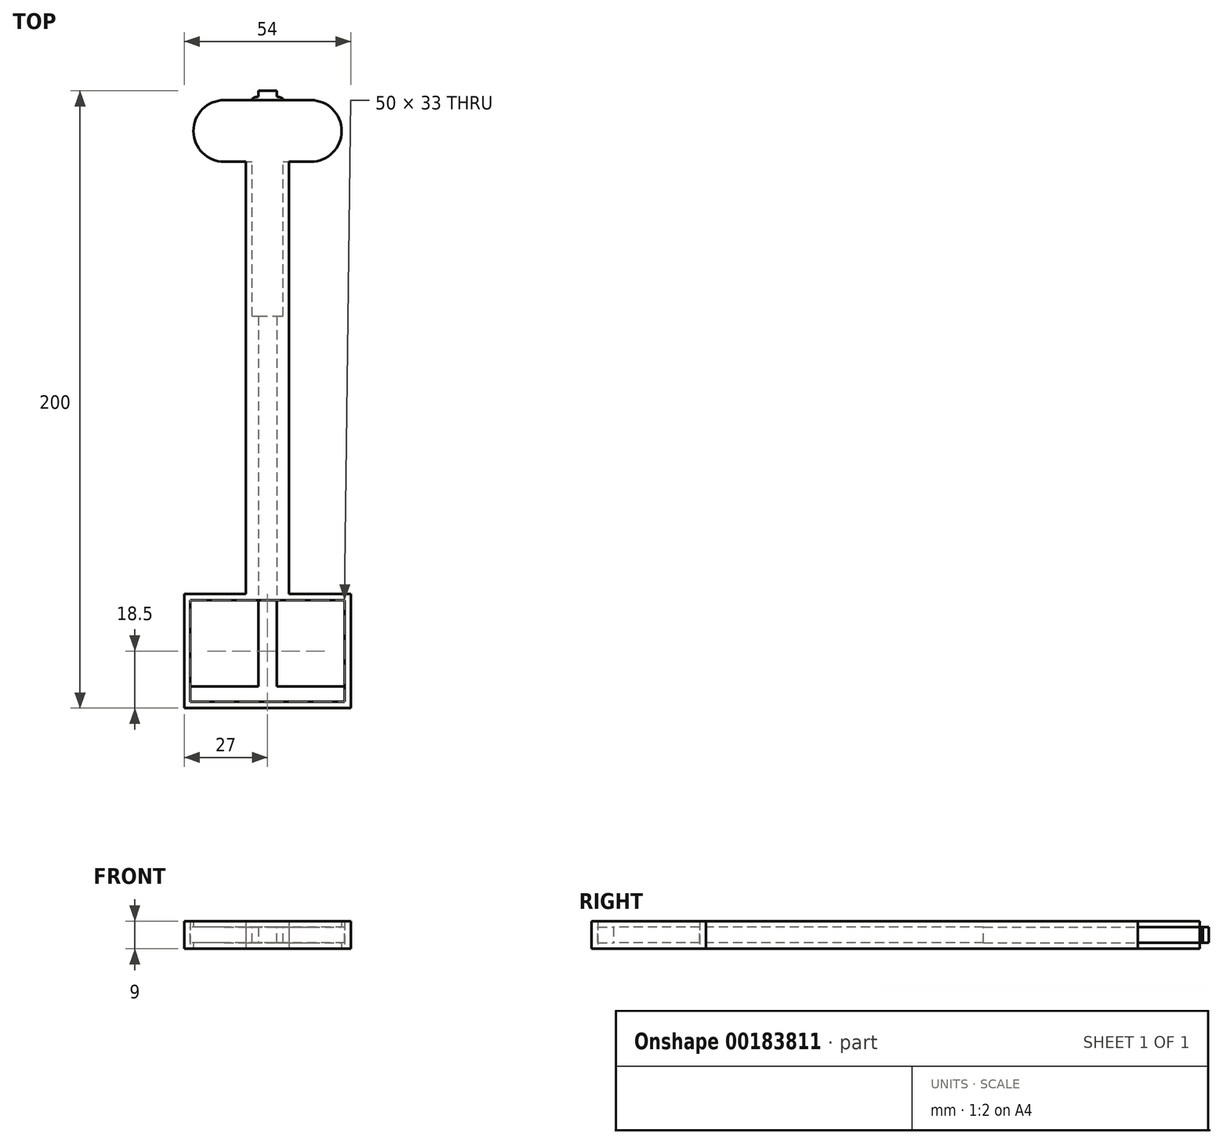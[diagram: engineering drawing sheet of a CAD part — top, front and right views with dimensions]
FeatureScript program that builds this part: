
annotation { "Feature Type Name" : "Feature", "Feature Type Description" : "" }
export const myFeature = defineFeature(function(context is Context, id is Id, definition is map)
    precondition{}
    {
        {
            var Q0;
            Q0=qCreatedBy(makeId("Top.planeOp"),FACE);
            var sketch = newSketch(context, id + "F0", { "sketchPlane" : qUnion([Q0])});
            skLineSegment(sketch, "E0.bottom", {"start": v(0, 13) * mm, "end": v(3, 13) * mm});
            skLineSegment(sketch, "E0.top", {"start": v(0, -180) * mm, "end": v(3, -180) * mm});
            skLineSegment(sketch, "E0.left", {"start": v(0, 13) * mm, "end": v(0, -180) * mm});
            skLineSegment(sketch, "E0.right", {"start": v(3, 13) * mm, "end": v(3, -180) * mm});
            skLineSegment(sketch, "E1", {"start": v(0, 10) * mm, "end": v(3, 10) * mm, "construction": true});
            skArc(sketch, "E2", {"start": v(3, 11.09) * mm, "mid": v(4.04, 10.94) * mm, "end": v(5, 10.5) * mm});
            skLineSegment(sketch, "E3", {"start": v(5, 10.5) * mm, "end": v(5, 10) * mm});
            skArc(sketch, "E4.MirrorCS", {"start": v(3, 8.91) * mm, "mid": v(4.04, 9.06) * mm, "end": v(5, 9.5) * mm});
            skLineSegment(sketch, "E5.MirrorCS", {"start": v(5, 9.5) * mm, "end": v(5, 10) * mm});
            skArc(sketch, "E6.1.0.0", {"start": v(3, 7.89) * mm, "mid": v(4.04, 7.74) * mm, "end": v(5, 7.3) * mm});
            skLineSegment(sketch, "E6.1.0.1", {"start": v(5, 7.3) * mm, "end": v(5, 6.8) * mm});
            skLineSegment(sketch, "E6.1.0.2", {"start": v(5, 6.3) * mm, "end": v(5, 6.8) * mm});
            skArc(sketch, "E6.1.0.3", {"start": v(3, 5.71) * mm, "mid": v(4.04, 5.86) * mm, "end": v(5, 6.3) * mm});
            skArc(sketch, "E6.2.0.0", {"start": v(3, 4.69) * mm, "mid": v(4.04, 4.54) * mm, "end": v(5, 4.1) * mm});
            skLineSegment(sketch, "E6.2.0.1", {"start": v(5, 4.1) * mm, "end": v(5, 3.6) * mm});
            skLineSegment(sketch, "E6.2.0.2", {"start": v(5, 3.1) * mm, "end": v(5, 3.6) * mm});
            skArc(sketch, "E6.2.0.3", {"start": v(3, 2.51) * mm, "mid": v(4.04, 2.66) * mm, "end": v(5, 3.1) * mm});
            skLineSegment(sketch, "E6.direction1", {"start": v(3, 7.39) * mm, "end": v(3, 4.19) * mm, "construction": true});
            skArc(sketch, "E7.0.3.0", {"start": v(3, 1.49) * mm, "mid": v(4.04, 1.34) * mm, "end": v(5, 0.9) * mm});
            skLineSegment(sketch, "E7.4.3.0", {"start": v(5, 0.9) * mm, "end": v(5, 0.4) * mm});
            skLineSegment(sketch, "E7.7.3.0", {"start": v(5, -0.1) * mm, "end": v(5, 0.4) * mm});
            skArc(sketch, "E7.10.3.0", {"start": v(3, -0.69) * mm, "mid": v(4.04, -0.54) * mm, "end": v(5, -0.1) * mm});
            skArc(sketch, "E7.0.4.0", {"start": v(3, -1.71) * mm, "mid": v(4.04, -1.86) * mm, "end": v(5, -2.3) * mm});
            skLineSegment(sketch, "E7.4.4.0", {"start": v(5, -2.3) * mm, "end": v(5, -2.8) * mm});
            skLineSegment(sketch, "E7.7.4.0", {"start": v(5, -3.3) * mm, "end": v(5, -2.8) * mm});
            skArc(sketch, "E7.10.4.0", {"start": v(3, -3.89) * mm, "mid": v(4.04, -3.74) * mm, "end": v(5, -3.3) * mm});
            skArc(sketch, "E7.0.5.0", {"start": v(3, -4.91) * mm, "mid": v(4.04, -5.06) * mm, "end": v(5, -5.5) * mm});
            skLineSegment(sketch, "E7.4.5.0", {"start": v(5, -5.5) * mm, "end": v(5, -6) * mm});
            skLineSegment(sketch, "E7.7.5.0", {"start": v(5, -6.5) * mm, "end": v(5, -6) * mm});
            skArc(sketch, "E7.10.5.0", {"start": v(3, -7.09) * mm, "mid": v(4.04, -6.94) * mm, "end": v(5, -6.5) * mm});
            skArc(sketch, "E7.0.6.0", {"start": v(3, -8.11) * mm, "mid": v(4.04, -8.26) * mm, "end": v(5, -8.7) * mm});
            skLineSegment(sketch, "E7.4.6.0", {"start": v(5, -8.7) * mm, "end": v(5, -9.2) * mm});
            skLineSegment(sketch, "E7.7.6.0", {"start": v(5, -9.7) * mm, "end": v(5, -9.2) * mm});
            skArc(sketch, "E7.10.6.0", {"start": v(3, -10.29) * mm, "mid": v(4.04, -10.14) * mm, "end": v(5, -9.7) * mm});
            skArc(sketch, "E7.0.7.0", {"start": v(3, -11.31) * mm, "mid": v(4.04, -11.46) * mm, "end": v(5, -11.9) * mm});
            skLineSegment(sketch, "E7.4.7.0", {"start": v(5, -11.9) * mm, "end": v(5, -12.4) * mm});
            skLineSegment(sketch, "E7.7.7.0", {"start": v(5, -12.9) * mm, "end": v(5, -12.4) * mm});
            skArc(sketch, "E7.10.7.0", {"start": v(3, -13.49) * mm, "mid": v(4.04, -13.34) * mm, "end": v(5, -12.9) * mm});
            skArc(sketch, "E7.0.8.0", {"start": v(3, -14.51) * mm, "mid": v(4.04, -14.66) * mm, "end": v(5, -15.1) * mm});
            skLineSegment(sketch, "E7.4.8.0", {"start": v(5, -15.1) * mm, "end": v(5, -15.6) * mm});
            skLineSegment(sketch, "E7.7.8.0", {"start": v(5, -16.1) * mm, "end": v(5, -15.6) * mm});
            skArc(sketch, "E7.10.8.0", {"start": v(3, -16.69) * mm, "mid": v(4.04, -16.54) * mm, "end": v(5, -16.1) * mm});
            skArc(sketch, "E7.0.9.0", {"start": v(3, -17.71) * mm, "mid": v(4.04, -17.86) * mm, "end": v(5, -18.3) * mm});
            skLineSegment(sketch, "E7.4.9.0", {"start": v(5, -18.3) * mm, "end": v(5, -18.8) * mm});
            skLineSegment(sketch, "E7.7.9.0", {"start": v(5, -19.3) * mm, "end": v(5, -18.8) * mm});
            skArc(sketch, "E7.10.9.0", {"start": v(3, -19.89) * mm, "mid": v(4.04, -19.74) * mm, "end": v(5, -19.3) * mm});
            skArc(sketch, "E7.0.10.0", {"start": v(3, -20.91) * mm, "mid": v(4.04, -21.06) * mm, "end": v(5, -21.5) * mm});
            skLineSegment(sketch, "E7.4.10.0", {"start": v(5, -21.5) * mm, "end": v(5, -22) * mm});
            skLineSegment(sketch, "E7.7.10.0", {"start": v(5, -22.5) * mm, "end": v(5, -22) * mm});
            skArc(sketch, "E7.10.10.0", {"start": v(3, -23.09) * mm, "mid": v(4.04, -22.94) * mm, "end": v(5, -22.5) * mm});
            skArc(sketch, "E7.0.11.0", {"start": v(3, -24.11) * mm, "mid": v(4.04, -24.26) * mm, "end": v(5, -24.7) * mm});
            skLineSegment(sketch, "E7.4.11.0", {"start": v(5, -24.7) * mm, "end": v(5, -25.2) * mm});
            skLineSegment(sketch, "E7.7.11.0", {"start": v(5, -25.7) * mm, "end": v(5, -25.2) * mm});
            skArc(sketch, "E7.10.11.0", {"start": v(3, -26.29) * mm, "mid": v(4.04, -26.14) * mm, "end": v(5, -25.7) * mm});
            skArc(sketch, "E7.0.12.0", {"start": v(3, -27.31) * mm, "mid": v(4.04, -27.46) * mm, "end": v(5, -27.9) * mm});
            skLineSegment(sketch, "E7.4.12.0", {"start": v(5, -27.9) * mm, "end": v(5, -28.4) * mm});
            skLineSegment(sketch, "E7.7.12.0", {"start": v(5, -28.9) * mm, "end": v(5, -28.4) * mm});
            skArc(sketch, "E7.10.12.0", {"start": v(3, -29.49) * mm, "mid": v(4.04, -29.34) * mm, "end": v(5, -28.9) * mm});
            skArc(sketch, "E7.0.13.0", {"start": v(3, -30.51) * mm, "mid": v(4.04, -30.66) * mm, "end": v(5, -31.1) * mm});
            skLineSegment(sketch, "E7.4.13.0", {"start": v(5, -31.1) * mm, "end": v(5, -31.6) * mm});
            skLineSegment(sketch, "E7.7.13.0", {"start": v(5, -32.1) * mm, "end": v(5, -31.6) * mm});
            skArc(sketch, "E7.10.13.0", {"start": v(3, -32.69) * mm, "mid": v(4.04, -32.54) * mm, "end": v(5, -32.1) * mm});
            skArc(sketch, "E7.0.14.0", {"start": v(3, -33.71) * mm, "mid": v(4.04, -33.86) * mm, "end": v(5, -34.3) * mm});
            skLineSegment(sketch, "E7.4.14.0", {"start": v(5, -34.3) * mm, "end": v(5, -34.8) * mm});
            skLineSegment(sketch, "E7.7.14.0", {"start": v(5, -35.3) * mm, "end": v(5, -34.8) * mm});
            skArc(sketch, "E7.10.14.0", {"start": v(3, -35.89) * mm, "mid": v(4.04, -35.74) * mm, "end": v(5, -35.3) * mm});
            skArc(sketch, "E7.0.15.0", {"start": v(3, -36.91) * mm, "mid": v(4.04, -37.06) * mm, "end": v(5, -37.5) * mm});
            skLineSegment(sketch, "E7.4.15.0", {"start": v(5, -37.5) * mm, "end": v(5, -38) * mm});
            skLineSegment(sketch, "E7.7.15.0", {"start": v(5, -38.5) * mm, "end": v(5, -38) * mm});
            skArc(sketch, "E7.10.15.0", {"start": v(3, -39.09) * mm, "mid": v(4.04, -38.94) * mm, "end": v(5, -38.5) * mm});
            skSolve(sketch);
        }
        {
            var Q0;
            Q0 = qSketchRegion(id + "F0", true);
            extrude(context, id + "F1", {"entities" : qUnion([Q0]), "depth" : 5 * mm});
        }
        {
            var Q0;
            Q0=makeQuery(id+"F1.opExtrude","SWEPT_BODY",BODY,{"disambiguationData":[OSD([sQuery(id+"F0.wireOp",EDGE,"E0.bottom"),sQuery(id+"F0.wireOp",EDGE,"E0.top"),sQuery(id+"F0.wireOp",EDGE,"E0.left"),sQuery(id+"F0.wireOp",EDGE,"E0.right"),sQuery(id+"F0.wireOp",EDGE,"E2"),sQuery(id+"F0.wireOp",EDGE,"E3"),sQuery(id+"F0.wireOp",EDGE,"E4.MirrorCS"),sQuery(id+"F0.wireOp",EDGE,"E5.MirrorCS"),sQuery(id+"F0.wireOp",EDGE,"E6.1.0.0"),sQuery(id+"F0.wireOp",EDGE,"E6.1.0.1"),sQuery(id+"F0.wireOp",EDGE,"E6.1.0.2"),sQuery(id+"F0.wireOp",EDGE,"E6.1.0.3"),sQuery(id+"F0.wireOp",EDGE,"E6.2.0.0"),sQuery(id+"F0.wireOp",EDGE,"E6.2.0.1"),sQuery(id+"F0.wireOp",EDGE,"E6.2.0.2"),sQuery(id+"F0.wireOp",EDGE,"E6.2.0.3"),sQuery(id+"F0.wireOp",EDGE,"E7.0.3.0"),sQuery(id+"F0.wireOp",EDGE,"E7.4.3.0"),sQuery(id+"F0.wireOp",EDGE,"E7.7.3.0"),sQuery(id+"F0.wireOp",EDGE,"E7.10.3.0"),sQuery(id+"F0.wireOp",EDGE,"E7.0.4.0"),sQuery(id+"F0.wireOp",EDGE,"E7.4.4.0"),sQuery(id+"F0.wireOp",EDGE,"E7.7.4.0"),sQuery(id+"F0.wireOp",EDGE,"E7.10.4.0"),sQuery(id+"F0.wireOp",EDGE,"E7.0.5.0"),sQuery(id+"F0.wireOp",EDGE,"E7.4.5.0"),sQuery(id+"F0.wireOp",EDGE,"E7.7.5.0"),sQuery(id+"F0.wireOp",EDGE,"E7.10.5.0"),sQuery(id+"F0.wireOp",EDGE,"E7.0.6.0"),sQuery(id+"F0.wireOp",EDGE,"E7.4.6.0"),sQuery(id+"F0.wireOp",EDGE,"E7.7.6.0"),sQuery(id+"F0.wireOp",EDGE,"E7.10.6.0"),sQuery(id+"F0.wireOp",EDGE,"E7.0.7.0"),sQuery(id+"F0.wireOp",EDGE,"E7.4.7.0"),sQuery(id+"F0.wireOp",EDGE,"E7.7.7.0"),sQuery(id+"F0.wireOp",EDGE,"E7.10.7.0"),sQuery(id+"F0.wireOp",EDGE,"E7.0.8.0"),sQuery(id+"F0.wireOp",EDGE,"E7.4.8.0"),sQuery(id+"F0.wireOp",EDGE,"E7.7.8.0"),sQuery(id+"F0.wireOp",EDGE,"E7.10.8.0"),sQuery(id+"F0.wireOp",EDGE,"E7.0.9.0"),sQuery(id+"F0.wireOp",EDGE,"E7.4.9.0"),sQuery(id+"F0.wireOp",EDGE,"E7.7.9.0"),sQuery(id+"F0.wireOp",EDGE,"E7.10.9.0"),sQuery(id+"F0.wireOp",EDGE,"E7.0.10.0"),sQuery(id+"F0.wireOp",EDGE,"E7.4.10.0"),sQuery(id+"F0.wireOp",EDGE,"E7.7.10.0"),sQuery(id+"F0.wireOp",EDGE,"E7.10.10.0"),sQuery(id+"F0.wireOp",EDGE,"E7.0.11.0"),sQuery(id+"F0.wireOp",EDGE,"E7.4.11.0"),sQuery(id+"F0.wireOp",EDGE,"E7.7.11.0"),sQuery(id+"F0.wireOp",EDGE,"E7.10.11.0"),sQuery(id+"F0.wireOp",EDGE,"E7.0.12.0"),sQuery(id+"F0.wireOp",EDGE,"E7.4.12.0"),sQuery(id+"F0.wireOp",EDGE,"E7.7.12.0"),sQuery(id+"F0.wireOp",EDGE,"E7.10.12.0"),sQuery(id+"F0.wireOp",EDGE,"E7.0.13.0"),sQuery(id+"F0.wireOp",EDGE,"E7.4.13.0"),sQuery(id+"F0.wireOp",EDGE,"E7.7.13.0"),sQuery(id+"F0.wireOp",EDGE,"E7.10.13.0"),sQuery(id+"F0.wireOp",EDGE,"E7.0.14.0"),sQuery(id+"F0.wireOp",EDGE,"E7.4.14.0"),sQuery(id+"F0.wireOp",EDGE,"E7.7.14.0"),sQuery(id+"F0.wireOp",EDGE,"E7.10.14.0"),sQuery(id+"F0.wireOp",EDGE,"E7.0.15.0"),sQuery(id+"F0.wireOp",EDGE,"E7.4.15.0"),sQuery(id+"F0.wireOp",EDGE,"E7.7.15.0"),sQuery(id+"F0.wireOp",EDGE,"E7.10.15.0")])]});
            var Q1;
            Q1=makeQuery(id+"F1.opExtrude","SWEPT_FACE",FACE,{"disambiguationData":[OSD([sQuery(id+"F0.wireOp",EDGE,"E0.left")])]});
            mirror(context, id + "F2", {"operationType" : NewBodyOperationType.ADD, "entities" : qUnion([Q0]), "mirrorPlane" : qUnion([Q1])});
        }
        {
            var Q0;
            {var subQ0=makeQuery(id+"F1.opExtrude","SWEPT_FACE",FACE,{"disambiguationData":[OSD([sQuery(id+"F0.wireOp",EDGE,"E0.top")])]});Q0=makeQuery(id+"F2.boolean.opBoolean","MERGE",FACE,{"derivedFrom":[subQ0,makeQuery(id+"F2.opPattern","COPY",FACE,{"derivedFrom":subQ0,"instanceName":"1"})]});}
            var sketch = newSketch(context, id + "F3", { "sketchPlane" : qUnion([Q0])});
            skLineSegment(sketch, "E8.bottom", {"start": v(25, 0) * mm, "end": v(-25, 0) * mm});
            skLineSegment(sketch, "E8.top", {"start": v(25, 5) * mm, "end": v(-25, 5) * mm});
            skLineSegment(sketch, "E8.left", {"start": v(25, 0) * mm, "end": v(25, 5) * mm});
            skLineSegment(sketch, "E8.right", {"start": v(-25, 0) * mm, "end": v(-25, 5) * mm});
            skPoint(sketch, "E8.middle", {"position": v(0, 2.5) * mm});
            skPoint(sketch, "E8.middle.positionSnap0", {"position": v(-3, 2.5) * mm});
            skPoint(sketch, "E8.centerSnap0", {"position": v(-3, 2.5) * mm});
            skSolve(sketch);
        }
        {
            var Q0;
            Q0 = qSketchRegion(id + "F3", true);
            extrude(context, id + "F4", {"entities" : qUnion([Q0]), "operationType" : NewBodyOperationType.ADD, "depth" : 5 * mm});
        }
        {
            var Q0;
            Q0=qCreatedBy(makeId("Top.planeOp"),FACE);
            var sketch = newSketch(context, id + "F5", { "sketchPlane" : qUnion([Q0])});
            skCircle(sketch, "E9", {"center": v(14, 0) * mm, "radius": 10 * mm});
            skLineSegment(sketch, "E10", {"start": v(0, 10) * mm, "end": v(14, 10) * mm});
            skLineSegment(sketch, "E11", {"start": v(14, -10) * mm, "end": v(7, -10) * mm});
            skLineSegment(sketch, "E12", {"start": v(7, -10) * mm, "end": v(7, -150) * mm});
            skLineSegment(sketch, "E13", {"start": v(7, -150) * mm, "end": v(27, -150) * mm});
            skLineSegment(sketch, "E14", {"start": v(27, -150) * mm, "end": v(27, -187) * mm});
            skLineSegment(sketch, "E15", {"start": v(27, -187) * mm, "end": v(0, -187) * mm});
            skLineSegment(sketch, "E16.MirrorCS", {"start": v(0, 10) * mm, "end": v(-14, 10) * mm});
            skCircle(sketch, "E17.MirrorC", {"center": v(-14, 0) * mm, "radius": 10 * mm});
            skLineSegment(sketch, "E18.MirrorCS", {"start": v(-14, -10) * mm, "end": v(-7, -10) * mm});
            skLineSegment(sketch, "E19.MirrorCS", {"start": v(-7, -10) * mm, "end": v(-7, -150) * mm});
            skLineSegment(sketch, "E20.MirrorCS", {"start": v(-7, -150) * mm, "end": v(-27, -150) * mm});
            skLineSegment(sketch, "E21.MirrorCS", {"start": v(-27, -150) * mm, "end": v(-27, -187) * mm});
            skLineSegment(sketch, "E22.MirrorCS", {"start": v(-27, -187) * mm, "end": v(0, -187) * mm});
            skLineSegment(sketch, "E23.bottom", {"start": v(25, -185) * mm, "end": v(-25, -185) * mm});
            skLineSegment(sketch, "E23.top", {"start": v(25, -152) * mm, "end": v(-25, -152) * mm});
            skLineSegment(sketch, "E23.left", {"start": v(25, -185) * mm, "end": v(25, -152) * mm});
            skLineSegment(sketch, "E23.right", {"start": v(-25, -185) * mm, "end": v(-25, -152) * mm});
            skPoint(sketch, "E23.middle", {"position": v(0, -168.5) * mm});
            skSolve(sketch);
        }
        {
            var Q0;
            Q0 = qSketchRegion(id + "F5", true);
            extrude(context, id + "F6", {"entities" : qUnion([Q0]), "depth" : 7 * mm, "hasSecondDirection" : true, "secondDirectionOppositeDirection" : true, "secondDirectionDepth" : 2 * mm});
        }
        {
            var Q0;
            Q0=makeQuery(id+"F1.opExtrude","SWEPT_BODY",BODY,{"disambiguationData":[OSD([sQuery(id+"F0.wireOp",EDGE,"E0.bottom"),sQuery(id+"F0.wireOp",EDGE,"E0.top"),sQuery(id+"F0.wireOp",EDGE,"E0.left"),sQuery(id+"F0.wireOp",EDGE,"E0.right"),sQuery(id+"F0.wireOp",EDGE,"E2"),sQuery(id+"F0.wireOp",EDGE,"E3"),sQuery(id+"F0.wireOp",EDGE,"E4.MirrorCS"),sQuery(id+"F0.wireOp",EDGE,"E5.MirrorCS"),sQuery(id+"F0.wireOp",EDGE,"E6.1.0.0"),sQuery(id+"F0.wireOp",EDGE,"E6.1.0.1"),sQuery(id+"F0.wireOp",EDGE,"E6.1.0.2"),sQuery(id+"F0.wireOp",EDGE,"E6.1.0.3"),sQuery(id+"F0.wireOp",EDGE,"E6.2.0.0"),sQuery(id+"F0.wireOp",EDGE,"E6.2.0.1"),sQuery(id+"F0.wireOp",EDGE,"E6.2.0.2"),sQuery(id+"F0.wireOp",EDGE,"E6.2.0.3"),sQuery(id+"F0.wireOp",EDGE,"E7.0.3.0"),sQuery(id+"F0.wireOp",EDGE,"E7.4.3.0"),sQuery(id+"F0.wireOp",EDGE,"E7.7.3.0"),sQuery(id+"F0.wireOp",EDGE,"E7.10.3.0"),sQuery(id+"F0.wireOp",EDGE,"E7.0.4.0"),sQuery(id+"F0.wireOp",EDGE,"E7.4.4.0"),sQuery(id+"F0.wireOp",EDGE,"E7.7.4.0"),sQuery(id+"F0.wireOp",EDGE,"E7.10.4.0"),sQuery(id+"F0.wireOp",EDGE,"E7.0.5.0"),sQuery(id+"F0.wireOp",EDGE,"E7.4.5.0"),sQuery(id+"F0.wireOp",EDGE,"E7.7.5.0"),sQuery(id+"F0.wireOp",EDGE,"E7.10.5.0"),sQuery(id+"F0.wireOp",EDGE,"E7.0.6.0"),sQuery(id+"F0.wireOp",EDGE,"E7.4.6.0"),sQuery(id+"F0.wireOp",EDGE,"E7.7.6.0"),sQuery(id+"F0.wireOp",EDGE,"E7.10.6.0"),sQuery(id+"F0.wireOp",EDGE,"E7.0.7.0"),sQuery(id+"F0.wireOp",EDGE,"E7.4.7.0"),sQuery(id+"F0.wireOp",EDGE,"E7.7.7.0"),sQuery(id+"F0.wireOp",EDGE,"E7.10.7.0"),sQuery(id+"F0.wireOp",EDGE,"E7.0.8.0"),sQuery(id+"F0.wireOp",EDGE,"E7.4.8.0"),sQuery(id+"F0.wireOp",EDGE,"E7.7.8.0"),sQuery(id+"F0.wireOp",EDGE,"E7.10.8.0"),sQuery(id+"F0.wireOp",EDGE,"E7.0.9.0"),sQuery(id+"F0.wireOp",EDGE,"E7.4.9.0"),sQuery(id+"F0.wireOp",EDGE,"E7.7.9.0"),sQuery(id+"F0.wireOp",EDGE,"E7.10.9.0"),sQuery(id+"F0.wireOp",EDGE,"E7.0.10.0"),sQuery(id+"F0.wireOp",EDGE,"E7.4.10.0"),sQuery(id+"F0.wireOp",EDGE,"E7.7.10.0"),sQuery(id+"F0.wireOp",EDGE,"E7.10.10.0"),sQuery(id+"F0.wireOp",EDGE,"E7.0.11.0"),sQuery(id+"F0.wireOp",EDGE,"E7.4.11.0"),sQuery(id+"F0.wireOp",EDGE,"E7.7.11.0"),sQuery(id+"F0.wireOp",EDGE,"E7.10.11.0"),sQuery(id+"F0.wireOp",EDGE,"E7.0.12.0"),sQuery(id+"F0.wireOp",EDGE,"E7.4.12.0"),sQuery(id+"F0.wireOp",EDGE,"E7.7.12.0"),sQuery(id+"F0.wireOp",EDGE,"E7.10.12.0"),sQuery(id+"F0.wireOp",EDGE,"E7.0.13.0"),sQuery(id+"F0.wireOp",EDGE,"E7.4.13.0"),sQuery(id+"F0.wireOp",EDGE,"E7.7.13.0"),sQuery(id+"F0.wireOp",EDGE,"E7.10.13.0"),sQuery(id+"F0.wireOp",EDGE,"E7.0.14.0"),sQuery(id+"F0.wireOp",EDGE,"E7.4.14.0"),sQuery(id+"F0.wireOp",EDGE,"E7.7.14.0"),sQuery(id+"F0.wireOp",EDGE,"E7.10.14.0"),sQuery(id+"F0.wireOp",EDGE,"E7.0.15.0"),sQuery(id+"F0.wireOp",EDGE,"E7.4.15.0"),sQuery(id+"F0.wireOp",EDGE,"E7.7.15.0"),sQuery(id+"F0.wireOp",EDGE,"E7.10.15.0")])]});
            var Q1;
            Q1=makeQuery(id+"F6.opExtrude","SWEPT_BODY",BODY,{"disambiguationData":[OSD([sQuery(id+"F5.wireOp",EDGE,"E9"),sQuery(id+"F5.wireOp",EDGE,"E10"),sQuery(id+"F5.wireOp",EDGE,"E11"),sQuery(id+"F5.wireOp",EDGE,"E12"),sQuery(id+"F5.wireOp",EDGE,"E13"),sQuery(id+"F5.wireOp",EDGE,"E14"),sQuery(id+"F5.wireOp",EDGE,"E15"),sQuery(id+"F5.wireOp",EDGE,"E16.MirrorCS"),sQuery(id+"F5.wireOp",EDGE,"E17.MirrorC"),sQuery(id+"F5.wireOp",EDGE,"E18.MirrorCS"),sQuery(id+"F5.wireOp",EDGE,"E19.MirrorCS"),sQuery(id+"F5.wireOp",EDGE,"E20.MirrorCS"),sQuery(id+"F5.wireOp",EDGE,"E21.MirrorCS"),sQuery(id+"F5.wireOp",EDGE,"E22.MirrorCS"),sQuery(id+"F5.wireOp",EDGE,"E23.bottom"),sQuery(id+"F5.wireOp",EDGE,"E23.top"),sQuery(id+"F5.wireOp",EDGE,"E23.left"),sQuery(id+"F5.wireOp",EDGE,"E23.right")])]});
            booleanBodies(context, id + "F7", {"operationType" : BooleanOperationType.SUBTRACTION, "tools" : qUnion([Q0]), "targets" : qUnion([Q1]), "keepTools" : true});
        }
        {
            var Q0;
            Q0=qCreatedBy(makeId("Top.planeOp"),FACE);
            var sketch = newSketch(context, id + "F8", { "sketchPlane" : qUnion([Q0])});
            skArc(sketch, "E24.0", {"start": v(-14, -10) * mm, "mid": v(-24, 0) * mm, "end": v(-14, 10) * mm});
            skLineSegment(sketch, "E25.0", {"start": v(-14, 10) * mm, "end": v(14, 10) * mm});
            skArc(sketch, "E26.0", {"start": v(14, -10) * mm, "mid": v(24, 0) * mm, "end": v(14, 10) * mm});
            skLineSegment(sketch, "E27", {"start": v(-14, -10) * mm, "end": v(14, -10) * mm});
            skSolve(sketch);
        }
        {
            var Q0;
            Q0 = qSketchRegion(id + "F8", true);
            extrude(context, id + "F9", {"entities" : qUnion([Q0]), "operationType" : NewBodyOperationType.REMOVE, "depth" : 5 * mm});
        }
        {
            var Q0;
            {var subQ69=sQuery(id+"F8.wireOp",EDGE,"E27");Q0=makeQuery(id+"F9.boolean.opBoolean","COPY",FACE,{"disambiguationData":[TD([makeQuery(id+"F6.opExtrude","SWEPT_FACE",FACE,{"disambiguationData":[OSD([sQuery(id+"F5.wireOp",EDGE,"E18.MirrorCS")])]})])],"derivedFrom":makeQuery(id+"F9.opExtrude","SWEPT_FACE",FACE,{"disambiguationData":[OSD([subQ69])]})});}
            var sketch = newSketch(context, id + "F10", { "sketchPlane" : qUnion([Q0])});
            skLineSegment(sketch, "E28.bottom", {"start": v(5, 0) * mm, "end": v(-5, 0) * mm});
            skLineSegment(sketch, "E28.top", {"start": v(5, 5) * mm, "end": v(-5, 5) * mm});
            skLineSegment(sketch, "E28.left", {"start": v(5, 0) * mm, "end": v(5, 5) * mm});
            skLineSegment(sketch, "E28.right", {"start": v(-5, 0) * mm, "end": v(-5, 5) * mm});
            skPoint(sketch, "E28.middle", {"position": v(0, 2.5) * mm});
            skSolve(sketch);
        }
        {
            var Q0;
            Q0 = qSketchRegion(id + "F10", true);
            extrude(context, id + "F11", {"entities" : qUnion([Q0]), "operationType" : NewBodyOperationType.REMOVE, "oppositeDirection" : true, "depth" : 50 * mm});
        }
    });
